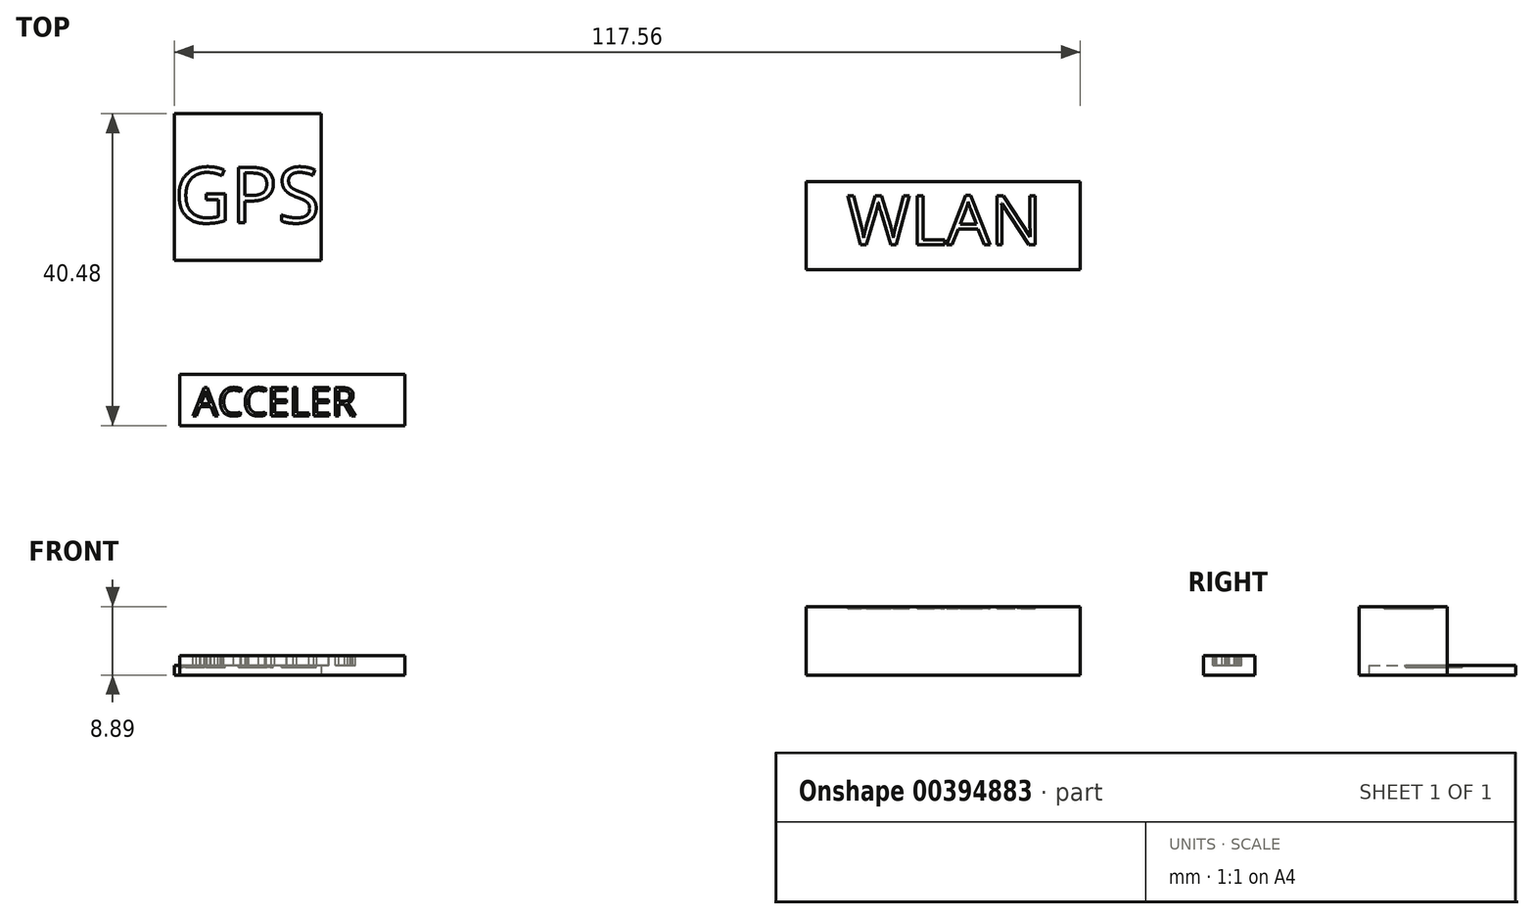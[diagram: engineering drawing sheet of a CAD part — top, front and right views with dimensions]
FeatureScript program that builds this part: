
annotation { "Feature Type Name" : "Feature", "Feature Type Description" : "" }
export const myFeature = defineFeature(function(context is Context, id is Id, definition is map)
    precondition{}
    {
        {
            var Q0;
            Q0=qCreatedBy(makeId("Top.planeOp"),FACE);
            var sketch = newSketch(context, id + "F0", { "sketchPlane" : qUnion([Q0])});
            skLineSegment(sketch, "E0.bottom", {"start": v(-56.6, -48.8) * mm, "end": v(-37.55, -48.8) * mm});
            skLineSegment(sketch, "E0.top", {"start": v(-56.6, -29.76) * mm, "end": v(-37.55, -29.76) * mm});
            skLineSegment(sketch, "E0.left", {"start": v(-56.6, -48.8) * mm, "end": v(-56.6, -29.76) * mm});
            skLineSegment(sketch, "E0.right", {"start": v(-37.55, -48.8) * mm, "end": v(-37.55, -29.76) * mm});
            skSolve(sketch);
        }
        {
            var Q0;
            Q0 = qSketchRegion(id + "F0", true);
            extrude(context, id + "F1", {"entities" : qUnion([Q0]), "depth" : 1.27 * mm});
        }
        {
            var Q0;
            Q0=makeQuery(id+"F1.opExtrude","CAP_FACE",FACE,{"disambiguationData":[OSD([sQuery(id+"F0.wireOp",EDGE,"E0.bottom"),sQuery(id+"F0.wireOp",EDGE,"E0.top"),sQuery(id+"F0.wireOp",EDGE,"E0.left"),sQuery(id+"F0.wireOp",EDGE,"E0.right")])],"isStart":false});
            var sketch = newSketch(context, id + "F2", { "sketchPlane" : qUnion([Q0])});
            skText(sketch, "E1", { "text": "GPS", "fontName": "OpenSans-Regular.ttf"});
            const initialGuessF2  = {"E1": [-0.0566, -0.04392, 1, 0, 0.00724]};
            skSetInitialGuess(sketch, initialGuessF2);
            skSolve(sketch);
        }
        {
            var Q0;
            Q0 = qSketchRegion(id + "F2", true);
            extrude(context, id + "F3", {"entities" : qUnion([Q0]), "operationType" : NewBodyOperationType.REMOVE, "oppositeDirection" : true, "depth" : 0.25 * mm});
        }
        {
            var Q0;
            Q0=qCreatedBy(makeId("Top.planeOp"),FACE);
            var sketch = newSketch(context, id + "F4", { "sketchPlane" : qUnion([Q0])});
            skLineSegment(sketch, "E2.bottom", {"start": v(25.4, -38.6) * mm, "end": v(60.96, -38.6) * mm});
            skLineSegment(sketch, "E2.top", {"start": v(25.4, -50.04) * mm, "end": v(60.96, -50.04) * mm});
            skLineSegment(sketch, "E2.left", {"start": v(25.4, -38.6) * mm, "end": v(25.4, -50.04) * mm});
            skLineSegment(sketch, "E2.right", {"start": v(60.96, -38.6) * mm, "end": v(60.96, -50.04) * mm});
            skSolve(sketch);
        }
        {
            var Q0;
            Q0 = qSketchRegion(id + "F4", true);
            extrude(context, id + "F5", {"entities" : qUnion([Q0]), "depth" : 8.9 * mm});
        }
        {
            var Q0;
            Q0=makeQuery(id+"F5.opExtrude","CAP_FACE",FACE,{"disambiguationData":[OSD([sQuery(id+"F4.wireOp",EDGE,"E2.bottom"),sQuery(id+"F4.wireOp",EDGE,"E2.top"),sQuery(id+"F4.wireOp",EDGE,"E2.left"),sQuery(id+"F4.wireOp",EDGE,"E2.right")])],"isStart":false});
            var sketch = newSketch(context, id + "F6", { "sketchPlane" : qUnion([Q0])});
            skText(sketch, "E3", { "text": "WLAN", "fontName": "OpenSans-Regular.ttf"});
            const initialGuessF6  = {"E3": [0.03064, -0.0468, 1, 0, 0.00645]};
            skSetInitialGuess(sketch, initialGuessF6);
            skSolve(sketch);
        }
        {
            var Q0;
            Q0 = qSketchRegion(id + "F6", true);
            extrude(context, id + "F7", {"entities" : qUnion([Q0]), "operationType" : NewBodyOperationType.REMOVE, "oppositeDirection" : true, "depth" : 0.25 * mm});
        }
        {
            var Q0;
            Q0=qCreatedBy(makeId("Top.planeOp"),FACE);
            var sketch = newSketch(context, id + "F8", { "sketchPlane" : qUnion([Q0])});
            skLineSegment(sketch, "E4.bottom", {"start": v(-55.9, -63.57) * mm, "end": v(-26.7, -63.57) * mm});
            skLineSegment(sketch, "E4.top", {"start": v(-55.9, -70.24) * mm, "end": v(-26.7, -70.24) * mm});
            skLineSegment(sketch, "E4.left", {"start": v(-55.9, -63.57) * mm, "end": v(-55.9, -70.24) * mm});
            skLineSegment(sketch, "E4.right", {"start": v(-26.7, -63.57) * mm, "end": v(-26.7, -70.24) * mm});
            skSolve(sketch);
        }
        {
            var Q0;
            Q0 = qSketchRegion(id + "F8", true);
            extrude(context, id + "F9", {"entities" : qUnion([Q0]), "depth" : 2.54 * mm});
        }
        {
            var Q0;
            Q0=makeQuery(id+"F9.opExtrude","CAP_FACE",FACE,{"disambiguationData":[OSD([sQuery(id+"F8.wireOp",EDGE,"E4.bottom"),sQuery(id+"F8.wireOp",EDGE,"E4.top"),sQuery(id+"F8.wireOp",EDGE,"E4.left"),sQuery(id+"F8.wireOp",EDGE,"E4.right")])],"isStart":false});
            var sketch = newSketch(context, id + "F10", { "sketchPlane" : qUnion([Q0])});
            skText(sketch, "E5", { "text": "ACCELER", "fontName": "OpenSans-Regular.ttf"});
            const initialGuessF10  = {"E5": [-0.05416, -0.06897, 1, 0, 0.00367]};
            skSetInitialGuess(sketch, initialGuessF10);
            skSolve(sketch);
        }
        {
            var Q0;
            Q0 = qSketchRegion(id + "F10", true);
            extrude(context, id + "F11", {"entities" : qUnion([Q0]), "operationType" : NewBodyOperationType.REMOVE, "oppositeDirection" : true, "depth" : 1.27 * mm});
        }
    });
